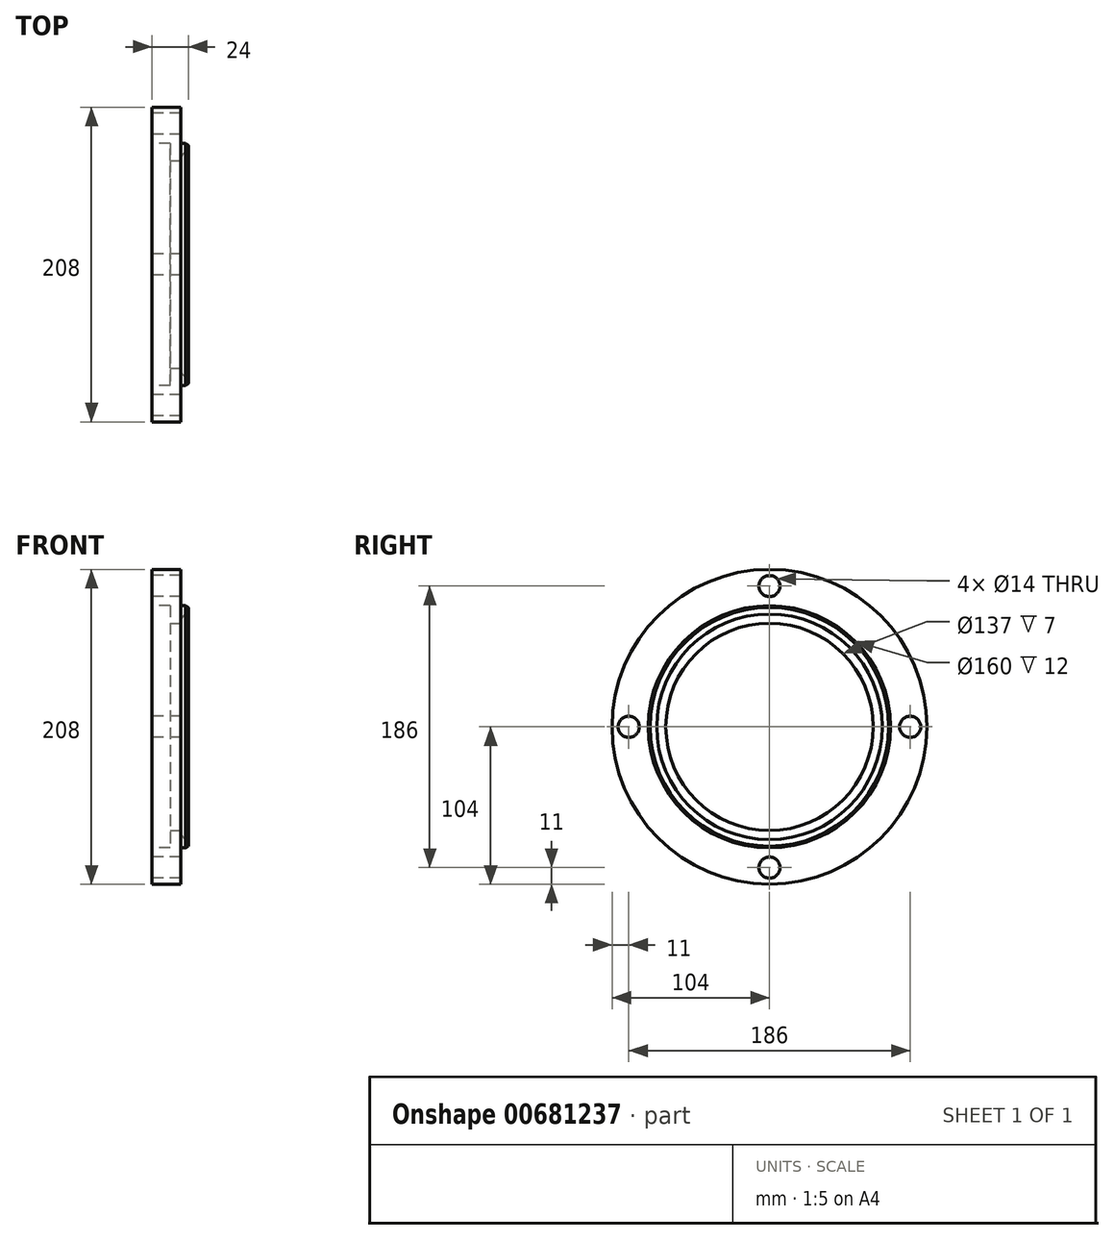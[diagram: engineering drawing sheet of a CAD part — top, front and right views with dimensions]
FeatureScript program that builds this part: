
annotation { "Feature Type Name" : "Feature", "Feature Type Description" : "" }
export const myFeature = defineFeature(function(context is Context, id is Id, definition is map)
    precondition{}
    {
        {
            var Q0;
            Q0=qCreatedBy(makeId("Right.planeOp"),FACE);
            var sketch = newSketch(context, id + "F0", { "sketchPlane" : qUnion([Q0])});
            skCircle(sketch, "E0", {"center": v(0, 0) * mm, "radius": 104 * mm});
            skCircle(sketch, "E1", {"center": v(0, 0) * mm, "radius": 68.5 * mm});
            skSolve(sketch);
        }
        {
            var Q0;
            Q0 = qSketchRegion(id + "F0", true);
            extrude(context, id + "F1", {"entities" : qUnion([Q0]), "oppositeDirection" : true, "depth" : 19 * mm, "offsetDistance" : 25 * mm});
        }
        {
            var Q0;
            Q0=makeQuery(id+"F1.opExtrude","CAP_FACE",FACE,{"disambiguationData":[OSD([sQuery(id+"F0.wireOp",EDGE,"E0"),sQuery(id+"F0.wireOp",EDGE,"E1")])],"isStart":true});
            var sketch = newSketch(context, id + "F2", { "sketchPlane" : qUnion([Q0])});
            skCircle(sketch, "E2", {"center": v(0, 0) * mm, "radius": 80 * mm});
            skCircle(sketch, "E3", {"center": v(0, 0) * mm, "radius": 74.5 * mm});
            skSolve(sketch);
        }
        {
            var Q0;
            Q0 = qSketchRegion(id + "F2", true);
            extrude(context, id + "F3", {"entities" : qUnion([Q0]), "operationType" : NewBodyOperationType.ADD, "depth" : 5 * mm, "offsetDistance" : 25 * mm});
        }
        {
            var Q0;
            Q0=makeQuery(id+"F1.opExtrude","CAP_FACE",FACE,{"disambiguationData":[OSD([sQuery(id+"F0.wireOp",EDGE,"E0"),sQuery(id+"F0.wireOp",EDGE,"E1")])],"isStart":false});
            var sketch = newSketch(context, id + "F4", { "sketchPlane" : qUnion([Q0])});
            skCircle(sketch, "E4", {"center": v(0, 0) * mm, "radius": 80 * mm});
            skSolve(sketch);
        }
        {
            var Q0;
            Q0 = qSketchRegion(id + "F4", true);
            extrude(context, id + "F5", {"entities" : qUnion([Q0]), "operationType" : NewBodyOperationType.REMOVE, "oppositeDirection" : true, "depth" : 12 * mm, "offsetDistance" : 25 * mm});
        }
        {
            var Q0;
            Q0=makeQuery(id+"F3.opExtrude","CAP_EDGE",EDGE,{"disambiguationData":[OSD([sQuery(id+"F2.wireOp",EDGE,"E2")])],"isStart":false});
            chamfer(context, id + "F6", {"entities" : qUnion([Q0]), "chamferType" : ChamferType.OFFSET_ANGLE, "width" : 2 * mm, "oppositeDirection" : true, "angle" : 30 * degree, "tangentPropagation" : true});
        }
        {
            var Q0;
            Q0=makeQuery(id+"F3.opExtrude","CAP_EDGE",EDGE,{"disambiguationData":[OSD([sQuery(id+"F2.wireOp",EDGE,"E3")])],"isStart":true});
            fillet(context, id + "F7", {"entities" : qUnion([Q0]), "radius" : 5 * mm, "tangentPropagation" : true, "allowEdgeOverflow" : false});
        }
        {
            var Q0;
            Q0=makeQuery(id+"F1.opExtrude","CAP_FACE",FACE,{"disambiguationData":[OSD([sQuery(id+"F0.wireOp",EDGE,"E0"),sQuery(id+"F0.wireOp",EDGE,"E1")])],"isStart":false});
            var sketch = newSketch(context, id + "F8", { "sketchPlane" : qUnion([Q0])});
            skCircle(sketch, "E5", {"center": v(0, 0) * mm, "radius": 93 * mm, "construction": true});
            skLineSegment(sketch, "E6", {"start": v(0, 0) * mm, "end": v(0, -93) * mm, "construction": true});
            skPoint(sketch, "E7", {"position": v(0, -93) * mm});
            skPoint(sketch, "E8.1.0", {"position": v(93, 0) * mm});
            skPoint(sketch, "E8.2.0", {"position": v(0, 93) * mm});
            skPoint(sketch, "E8.3.0", {"position": v(-93, 0) * mm});
            skSolve(sketch);
        }
        {
            var Q0;
            Q0=sQuery(id+"F8.wireOp",VERTEX,"E7");
            var Q1;
            Q1=sQuery(id+"F8.wireOp",VERTEX,"E8.3.0");
            var Q2;
            Q2=sQuery(id+"F8.wireOp",VERTEX,"E8.2.0");
            var Q3;
            Q3=sQuery(id+"F8.wireOp",VERTEX,"E8.1.0");
            var Q4;
            Q4=makeQuery(id+"F1.opExtrude","SWEPT_BODY",BODY,{"disambiguationData":[OSD([sQuery(id+"F0.wireOp",EDGE,"E0"),sQuery(id+"F0.wireOp",EDGE,"E1")])]});
            hole(context, id + "F9", {"style" : HoleStyle.SIMPLE, "endStyle" : HoleEndStyle.BLIND, "standardTappedOrClearance" : lookupTablePath({ "standard" : "ISO", "size" : "14", "type" : "Drilled" }), "standardBlindInLast" : lookupTablePath({ "standard" : "ISO", "size" : "14", "type" : "Drilled" }), "holeDiameter" : 14 * mm, "majorDiameter" : 10 * mm, "holeDepth" : 25.5 * mm, "isTappedThrough" : true, "tappedDepth" : 21 * mm, "tapClearance" : 3, "locations" : qUnion([Q0, Q1, Q2, Q3]), "scope" : qUnion([Q4])});
        }
    });
